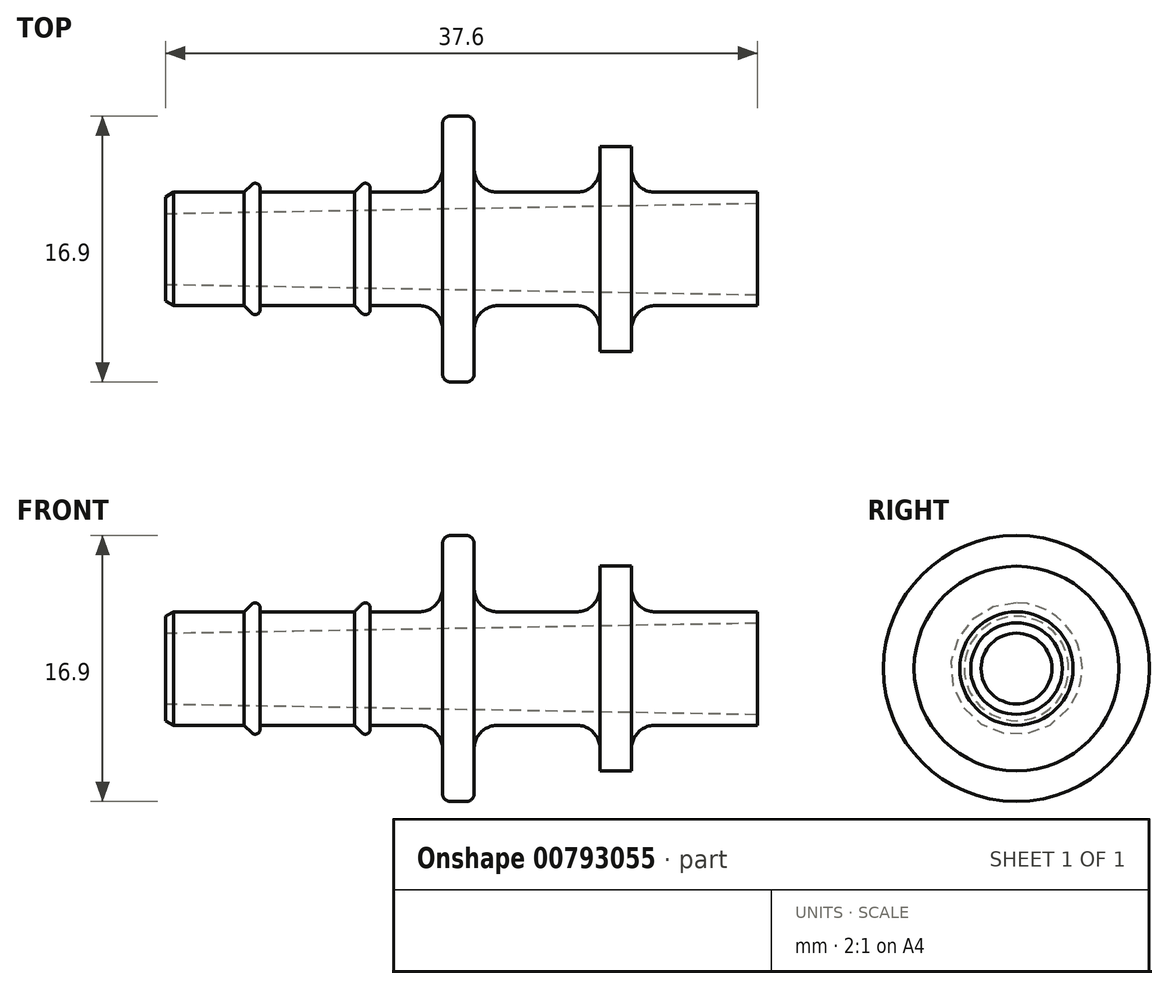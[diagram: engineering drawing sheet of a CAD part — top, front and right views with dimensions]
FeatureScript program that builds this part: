
annotation { "Feature Type Name" : "Feature", "Feature Type Description" : "" }
export const myFeature = defineFeature(function(context is Context, id is Id, definition is map)
    precondition{}
    {
        {
            var Q0;
            Q0=qCreatedBy(makeId("Front.planeOp"),FACE);
            var sketch = newSketch(context, id + "F0", { "sketchPlane" : qUnion([Q0])});
            skLineSegment(sketch, "E0", {"start": v(-18.8, -2.25) * mm, "end": v(-18.8, -3.31) * mm});
            skLineSegment(sketch, "E1", {"start": v(-18.3, -3.6) * mm, "end": v(-13.8, -3.6) * mm});
            skLineSegment(sketch, "E2", {"start": v(-12.8, -3.88) * mm, "end": v(-12.8, -3.6) * mm});
            skLineSegment(sketch, "E3", {"start": v(-12.8, -3.6) * mm, "end": v(-6.8, -3.6) * mm});
            skLineSegment(sketch, "E4", {"start": v(-5.8, -3.6) * mm, "end": v(-2.7, -3.6) * mm});
            skLineSegment(sketch, "E5", {"start": v(-1.2, -5.1) * mm, "end": v(-1.2, -7.95) * mm});
            skLineSegment(sketch, "E6", {"start": v(-0.7, -8.45) * mm, "end": v(0.3, -8.45) * mm});
            skLineSegment(sketch, "E7", {"start": v(0.8, -7.95) * mm, "end": v(0.8, -5.1) * mm});
            skLineSegment(sketch, "E8", {"start": v(2.3, -3.6) * mm, "end": v(7.3, -3.6) * mm});
            skLineSegment(sketch, "E9", {"start": v(8.8, -5.1) * mm, "end": v(8.8, -6.5) * mm});
            skLineSegment(sketch, "E10", {"start": v(8.8, -6.5) * mm, "end": v(10.8, -6.5) * mm});
            skLineSegment(sketch, "E11", {"start": v(10.8, -6.5) * mm, "end": v(10.8, -5.1) * mm});
            skLineSegment(sketch, "E12", {"start": v(12.3, -3.6) * mm, "end": v(18.8, -3.6) * mm});
            skLineSegment(sketch, "E13", {"start": v(18.8, -3.6) * mm, "end": v(18.8, -2.9) * mm});
            skLineSegment(sketch, "E14", {"start": v(-18.9, 0) * mm, "end": v(18.8, 0) * mm, "construction": true});
            skLineSegment(sketch, "E15", {"start": v(-13.8, -3.6) * mm, "end": v(-13.31, -4.09) * mm});
            skPoint(sketch, "E16.orphan", {"position": v(-12.8, -4.82) * mm});
            skArc(sketch, "E17.filletArc", {"start": v(-13.31, -4.09) * mm, "mid": v(-12.99, -4.15) * mm, "end": v(-12.8, -3.88) * mm});
            skLineSegment(sketch, "E18", {"start": v(-6.8, -3.6) * mm, "end": v(-6.31, -4.09) * mm});
            skLineSegment(sketch, "E19", {"start": v(-5.8, -3.6) * mm, "end": v(-5.8, -3.88) * mm});
            skPoint(sketch, "E20.visualSharp", {"position": v(-5.8, -4.6) * mm});
            skArc(sketch, "E20.filletArc", {"start": v(-6.31, -4.09) * mm, "mid": v(-5.99, -4.15) * mm, "end": v(-5.8, -3.88) * mm});
            skPoint(sketch, "E21.visualSharp", {"position": v(0.8, -3.6) * mm});
            skArc(sketch, "E21.filletArc", {"start": v(2.3, -3.6) * mm, "mid": v(1.24, -4.04) * mm, "end": v(0.8, -5.1) * mm});
            skPoint(sketch, "E22.visualSharp", {"position": v(-1.2, -3.6) * mm});
            skArc(sketch, "E22.filletArc", {"start": v(-1.2, -5.1) * mm, "mid": v(-1.64, -4.04) * mm, "end": v(-2.7, -3.6) * mm});
            skPoint(sketch, "E23.visualSharp", {"position": v(0.8, -8.45) * mm});
            skArc(sketch, "E23.filletArc", {"start": v(0.3, -8.45) * mm, "mid": v(0.65, -8.3) * mm, "end": v(0.8, -7.95) * mm});
            skPoint(sketch, "E24.visualSharp", {"position": v(-1.2, -8.45) * mm});
            skArc(sketch, "E24.filletArc", {"start": v(-1.2, -7.95) * mm, "mid": v(-1.05, -8.3) * mm, "end": v(-0.7, -8.45) * mm});
            skPoint(sketch, "E25.visualSharp", {"position": v(10.8, -3.6) * mm});
            skArc(sketch, "E25.filletArc", {"start": v(12.3, -3.6) * mm, "mid": v(11.24, -4.04) * mm, "end": v(10.8, -5.1) * mm});
            skPoint(sketch, "E26.visualSharp", {"position": v(8.8, -3.6) * mm});
            skArc(sketch, "E26.filletArc", {"start": v(8.8, -5.1) * mm, "mid": v(8.36, -4.04) * mm, "end": v(7.3, -3.6) * mm});
            skLineSegment(sketch, "E27", {"start": v(-18.3, -3.6) * mm, "end": v(-18.8, -3.31) * mm});
            skPoint(sketch, "E28.orphan", {"position": v(-18.8, -3.6) * mm});
            skPoint(sketch, "E29.orphan", {"position": v(-18.8, 0) * mm});
            skPoint(sketch, "E30.orphan", {"position": v(18.8, 0) * mm});
            skLineSegment(sketch, "E31", {"start": v(-18.8, -2.25) * mm, "end": v(18.8, -2.9) * mm});
            skSolve(sketch);
        }
        {
            var Q0;
            Q0 = qSketchRegion(id + "F0", true);
            var Q1;
            Q1=sQuery(id+"F0.wireOp",EDGE,"E14");
            revolve(context, id + "F1", {"surfaceOperationType" : NewSurfaceOperationType.NEW, "entities" : qUnion([Q0]), "axis" : qUnion([Q1]), "revolveType" : RevolveType.FULL});
        }
    });
